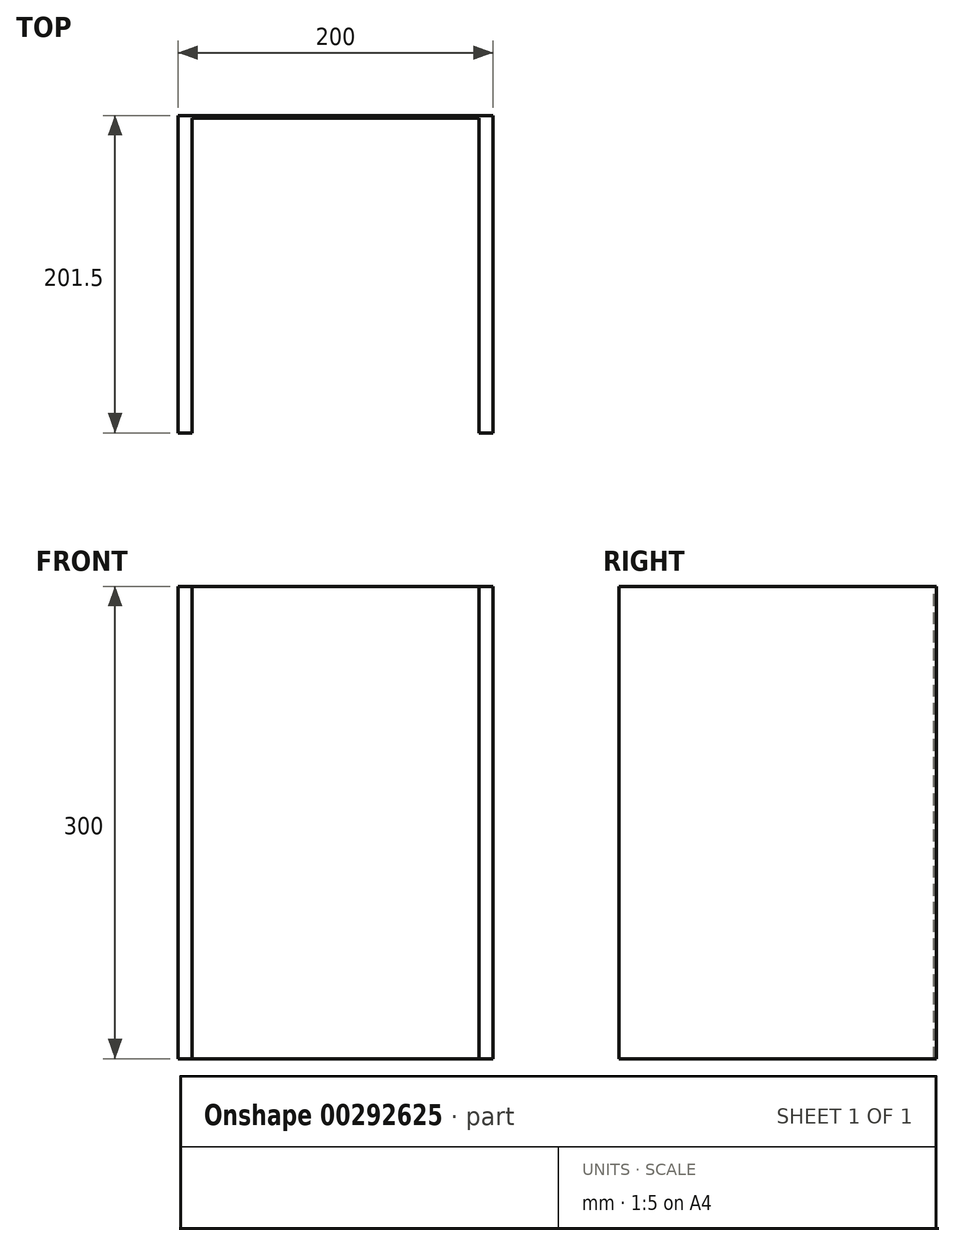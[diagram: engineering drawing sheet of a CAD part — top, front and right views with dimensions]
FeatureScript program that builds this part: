
annotation { "Feature Type Name" : "Feature", "Feature Type Description" : "" }
export const myFeature = defineFeature(function(context is Context, id is Id, definition is map)
    precondition{}
    {
        {
            var Q0;
            Q0=qCreatedBy(makeId("Front.planeOp"),FACE);
            var sketch = newSketch(context, id + "F0", { "sketchPlane" : qUnion([Q0])});
            skLineSegment(sketch, "E0.bottom", {"start": v(0, 0) * mm, "end": v(200, 0) * mm});
            skLineSegment(sketch, "E0.top", {"start": v(0, 300) * mm, "end": v(200, 300) * mm});
            skLineSegment(sketch, "E0.left", {"start": v(0, 0) * mm, "end": v(0, 300) * mm});
            skLineSegment(sketch, "E0.right", {"start": v(200, 0) * mm, "end": v(200, 300) * mm});
            skSolve(sketch);
        }
        {
            var Q0;
            Q0=makeQuery(id+"F0.imprint","IMPRINT",FACE,{"disambiguationData":[TD([[makeQuery(id+"F0.imprint","IMPRINT",EDGE,{"derivedFrom":sQuery(id+"F0.wireOp",EDGE,"E0.bottom")}),1.0]])]});
            extrude(context, id + "F1", {"entities" : qUnion([Q0]), "depth" : 1.5 * mm});
        }
        {
            var Q0;
            Q0=makeQuery(id+"F1.opExtrude","CAP_FACE",FACE,{"disambiguationData":[OSD([sQuery(id+"F0.wireOp",EDGE,"E0.bottom"),sQuery(id+"F0.wireOp",EDGE,"E0.top"),sQuery(id+"F0.wireOp",EDGE,"E0.left"),sQuery(id+"F0.wireOp",EDGE,"E0.right")])],"isStart":false});
            var sketch = newSketch(context, id + "F2", { "sketchPlane" : qUnion([Q0])});
            skLineSegment(sketch, "E1.bottom", {"start": v(0, 0) * mm, "end": v(9, 0) * mm});
            skLineSegment(sketch, "E1.top", {"start": v(0, 300) * mm, "end": v(9, 300) * mm});
            skLineSegment(sketch, "E1.left", {"start": v(0, 0) * mm, "end": v(0, 300) * mm});
            skLineSegment(sketch, "E1.right", {"start": v(9, 0) * mm, "end": v(9, 300) * mm});
            skSolve(sketch);
        }
        {
            var Q0;
            Q0 = qSketchRegion(id + "F2", true);
            extrude(context, id + "F3", {"entities" : qUnion([Q0]), "operationType" : NewBodyOperationType.ADD, "depth" : 200 * mm});
        }
        {
            var Q0;
            Q0=makeQuery(id+"F1.opExtrude","CAP_FACE",FACE,{"disambiguationData":[OSD([sQuery(id+"F0.wireOp",EDGE,"E0.bottom"),sQuery(id+"F0.wireOp",EDGE,"E0.top"),sQuery(id+"F0.wireOp",EDGE,"E0.left"),sQuery(id+"F0.wireOp",EDGE,"E0.right")])],"isStart":false});
            var sketch = newSketch(context, id + "F4", { "sketchPlane" : qUnion([Q0])});
            skLineSegment(sketch, "E2.bottom", {"start": v(200, 0) * mm, "end": v(191, 0) * mm});
            skLineSegment(sketch, "E2.top", {"start": v(200, 300) * mm, "end": v(191, 300) * mm});
            skLineSegment(sketch, "E2.left", {"start": v(200, 0) * mm, "end": v(200, 300) * mm});
            skLineSegment(sketch, "E2.right", {"start": v(191, 0) * mm, "end": v(191, 300) * mm});
            skSolve(sketch);
        }
        {
            var Q0;
            Q0 = qSketchRegion(id + "F4", true);
            extrude(context, id + "F5", {"entities" : qUnion([Q0]), "operationType" : NewBodyOperationType.ADD, "depth" : 200 * mm});
        }
    });
